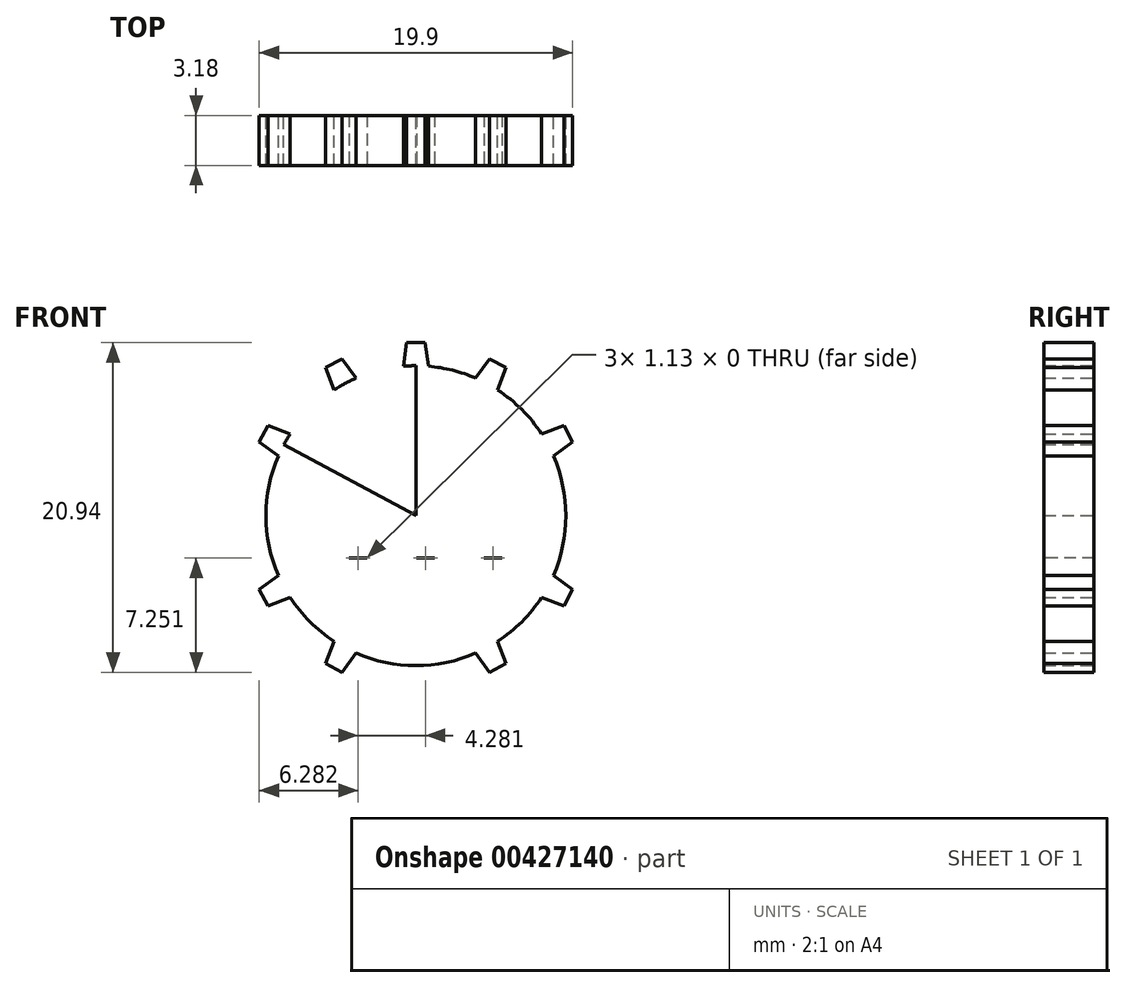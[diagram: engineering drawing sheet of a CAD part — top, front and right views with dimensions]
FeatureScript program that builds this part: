
annotation { "Feature Type Name" : "Feature", "Feature Type Description" : "" }
export const myFeature = defineFeature(function(context is Context, id is Id, definition is map)
    precondition{}
    {
        {
            var Q0;
            Q0=qCreatedBy(makeId("Front.planeOp"),FACE);
            var sketch = newSketch(context, id + "F0", { "sketchPlane" : qUnion([Q0])});
            skCircle(sketch, "E0", {"center": v(0, 0) * mm, "radius": 9.52 * mm});
            skLineSegment(sketch, "E1", {"start": v(0, 13.24) * mm, "end": v(0, -13.24) * mm});
            skLineSegment(sketch, "E2", {"start": v(-13.24, 0) * mm, "end": v(13.24, 0) * mm});
            skLineSegment(sketch, "E3", {"start": v(0, 0) * mm, "end": v(-5.21, 9.68) * mm});
            skLineSegment(sketch, "E4", {"start": v(0, 0) * mm, "end": v(5.21, -9.68) * mm});
            skLineSegment(sketch, "E5", {"start": v(0, 0) * mm, "end": v(5.21, 9.68) * mm});
            skLineSegment(sketch, "E6", {"start": v(0, 0) * mm, "end": v(-5.21, -9.68) * mm});
            skLineSegment(sketch, "E7", {"start": v(0, 0) * mm, "end": v(-9.68, 5.21) * mm});
            skLineSegment(sketch, "E8", {"start": v(0, 0) * mm, "end": v(9.68, -5.21) * mm});
            skLineSegment(sketch, "E9", {"start": v(0, 0) * mm, "end": v(9.68, 5.21) * mm});
            skLineSegment(sketch, "E10", {"start": v(0, 0) * mm, "end": v(-9.68, -5.21) * mm});
            skLineSegment(sketch, "E11", {"start": v(-5.21, 9.68) * mm, "end": v(-5.73, 9.4) * mm});
            skLineSegment(sketch, "E12", {"start": v(-5.73, 9.4) * mm, "end": v(-5.2, 7.98) * mm});
            skLineSegment(sketch, "E13", {"start": v(-5.21, 9.68) * mm, "end": v(-4.7, 9.95) * mm});
            skLineSegment(sketch, "E14", {"start": v(-4.7, 9.95) * mm, "end": v(-3.8, 8.73) * mm});
            skLineSegment(sketch, "E15", {"start": v(-9.68, 5.21) * mm, "end": v(-9.4, 5.73) * mm});
            skLineSegment(sketch, "E16", {"start": v(-9.68, 5.21) * mm, "end": v(-9.95, 4.7) * mm});
            skLineSegment(sketch, "E17", {"start": v(-9.4, 5.73) * mm, "end": v(-7.98, 5.2) * mm});
            skLineSegment(sketch, "E18", {"start": v(-9.95, 4.7) * mm, "end": v(-8.73, 3.8) * mm});
            skLineSegment(sketch, "E19", {"start": v(5.21, 9.68) * mm, "end": v(4.7, 9.95) * mm});
            skLineSegment(sketch, "E20", {"start": v(5.21, 9.68) * mm, "end": v(5.73, 9.4) * mm});
            skLineSegment(sketch, "E21", {"start": v(4.7, 9.95) * mm, "end": v(3.8, 8.73) * mm});
            skLineSegment(sketch, "E22", {"start": v(5.73, 9.4) * mm, "end": v(5.2, 7.98) * mm});
            skLineSegment(sketch, "E23", {"start": v(9.68, 5.21) * mm, "end": v(9.4, 5.73) * mm});
            skLineSegment(sketch, "E24", {"start": v(9.68, 5.21) * mm, "end": v(9.95, 4.7) * mm});
            skLineSegment(sketch, "E25", {"start": v(9.4, 5.73) * mm, "end": v(7.98, 5.2) * mm});
            skLineSegment(sketch, "E26", {"start": v(9.95, 4.7) * mm, "end": v(8.73, 3.8) * mm});
            skLineSegment(sketch, "E27", {"start": v(0, 10.99) * mm, "end": v(-0.59, 10.99) * mm});
            skLineSegment(sketch, "E28", {"start": v(0, 10.99) * mm, "end": v(0.59, 10.99) * mm});
            skLineSegment(sketch, "E29", {"start": v(0.59, 10.99) * mm, "end": v(0.8, 9.5) * mm});
            skLineSegment(sketch, "E30", {"start": v(-0.59, 10.99) * mm, "end": v(-0.8, 9.5) * mm});
            skLineSegment(sketch, "E31", {"start": v(0, 10.99) * mm, "end": v(0, 9.52) * mm});
            skLineSegment(sketch, "E32", {"start": v(-5.21, 9.68) * mm, "end": v(-4.52, 8.39) * mm});
            skLineSegment(sketch, "E33", {"start": v(-9.52, 0) * mm, "end": v(-10.99, 0) * mm});
            skLineSegment(sketch, "E34", {"start": v(-10.99, 0) * mm, "end": v(-10.99, -0.59) * mm});
            skLineSegment(sketch, "E35", {"start": v(-10.99, 0) * mm, "end": v(-10.99, 0.59) * mm});
            skLineSegment(sketch, "E36", {"start": v(-10.99, -0.59) * mm, "end": v(-9.5, -0.8) * mm});
            skLineSegment(sketch, "E37", {"start": v(-10.99, 0.59) * mm, "end": v(-9.5, 0.8) * mm});
            skLineSegment(sketch, "E38", {"start": v(9.52, 0) * mm, "end": v(10.99, 0) * mm});
            skLineSegment(sketch, "E39", {"start": v(10.99, 0) * mm, "end": v(10.99, 0.59) * mm});
            skLineSegment(sketch, "E40", {"start": v(10.99, 0) * mm, "end": v(10.99, -0.59) * mm});
            skLineSegment(sketch, "E41", {"start": v(10.99, 0.59) * mm, "end": v(9.5, 0.8) * mm});
            skLineSegment(sketch, "E42", {"start": v(10.99, -0.59) * mm, "end": v(9.5, -0.8) * mm});
            skLineSegment(sketch, "E43", {"start": v(9.68, -5.21) * mm, "end": v(9.95, -4.7) * mm});
            skLineSegment(sketch, "E44", {"start": v(9.68, -5.21) * mm, "end": v(9.4, -5.73) * mm});
            skLineSegment(sketch, "E45", {"start": v(9.95, -4.7) * mm, "end": v(8.73, -3.8) * mm});
            skLineSegment(sketch, "E46", {"start": v(9.4, -5.73) * mm, "end": v(7.98, -5.2) * mm});
            skLineSegment(sketch, "E47", {"start": v(-9.68, -5.21) * mm, "end": v(-9.95, -4.7) * mm});
            skLineSegment(sketch, "E48", {"start": v(-9.68, -5.21) * mm, "end": v(-9.4, -5.73) * mm});
            skLineSegment(sketch, "E49", {"start": v(-9.95, -4.7) * mm, "end": v(-8.73, -3.8) * mm});
            skLineSegment(sketch, "E50", {"start": v(-9.4, -5.73) * mm, "end": v(-7.98, -5.2) * mm});
            skLineSegment(sketch, "E51", {"start": v(-5.21, -9.68) * mm, "end": v(-5.73, -9.4) * mm});
            skLineSegment(sketch, "E52", {"start": v(-5.21, -9.68) * mm, "end": v(-4.7, -9.95) * mm});
            skLineSegment(sketch, "E53", {"start": v(-5.73, -9.4) * mm, "end": v(-5.2, -7.98) * mm});
            skLineSegment(sketch, "E54", {"start": v(-4.7, -9.95) * mm, "end": v(-3.8, -8.73) * mm});
            skLineSegment(sketch, "E55", {"start": v(0, -9.52) * mm, "end": v(0, -10.99) * mm});
            skLineSegment(sketch, "E56", {"start": v(0, -10.99) * mm, "end": v(-0.59, -10.99) * mm});
            skLineSegment(sketch, "E57", {"start": v(0, -10.99) * mm, "end": v(0.59, -10.99) * mm});
            skLineSegment(sketch, "E58", {"start": v(-0.59, -10.99) * mm, "end": v(-0.8, -9.5) * mm});
            skLineSegment(sketch, "E59", {"start": v(0.59, -10.99) * mm, "end": v(0.8, -9.5) * mm});
            skLineSegment(sketch, "E60", {"start": v(5.21, -9.68) * mm, "end": v(4.7, -9.95) * mm});
            skLineSegment(sketch, "E61", {"start": v(5.21, -9.68) * mm, "end": v(5.73, -9.4) * mm});
            skLineSegment(sketch, "E62", {"start": v(4.7, -9.95) * mm, "end": v(3.8, -8.73) * mm});
            skLineSegment(sketch, "E63", {"start": v(5.73, -9.4) * mm, "end": v(5.2, -7.98) * mm});
            skSolve(sketch);
        }
        {
            var Q0;
            {var subQ3=sQuery(id+"F0.wireOp",EDGE,"E0");var subQ5=makeQuery(id+"F0.imprint","INTERSECT",VERTEX,{"derivedFrom":[subQ3,sQuery(id+"F0.wireOp",EDGE,"E18")]});Q0=makeQuery(id+"F0.imprint","IMPRINT",FACE,{"disambiguationData":[TD([[makeQuery(id+"F0.imprint","IMPRINT",EDGE,{"disambiguationData":[TD([[subQ5,1.0]])],"derivedFrom":subQ3}),1.0]])]});}
            var Q1;
            {var subQ0=sQuery(id+"F0.wireOp",EDGE,"E3");Q1=makeQuery(id+"F0.imprint","IMPRINT",FACE,{"disambiguationData":[TD([[makeQuery(id+"F0.imprint","IMPRINT",EDGE,{"derivedFrom":subQ0}),1.0]])]});}
            var Q2;
            {var subQ0=sQuery(id+"F0.wireOp",EDGE,"E0");var subQ4=makeQuery(id+"F0.imprint","INTERSECT",VERTEX,{"derivedFrom":[subQ0,sQuery(id+"F0.wireOp",EDGE,"E21")]});Q2=makeQuery(id+"F0.imprint","IMPRINT",FACE,{"disambiguationData":[TD([[makeQuery(id+"F0.imprint","IMPRINT",EDGE,{"disambiguationData":[TD([[subQ4,1.0]])],"derivedFrom":subQ0}),1.0]])]});}
            var Q3;
            {var subQ0=sQuery(id+"F0.wireOp",EDGE,"E3");Q3=makeQuery(id+"F0.imprint","IMPRINT",FACE,{"disambiguationData":[TD([[makeQuery(id+"F0.imprint","IMPRINT",EDGE,{"derivedFrom":subQ0}),-1.0]])]});}
            var Q4;
            {var subQ0=sQuery(id+"F0.wireOp",EDGE,"E0");var subQ4=makeQuery(id+"F0.imprint","INTERSECT",VERTEX,{"derivedFrom":[subQ0,sQuery(id+"F0.wireOp",EDGE,"E25")]});Q4=makeQuery(id+"F0.imprint","IMPRINT",FACE,{"disambiguationData":[TD([[makeQuery(id+"F0.imprint","IMPRINT",EDGE,{"disambiguationData":[TD([[subQ4,1.0]])],"derivedFrom":subQ0}),1.0]])]});}
            var Q5;
            {var subQ3=sQuery(id+"F0.wireOp",EDGE,"E0");var subQ5=makeQuery(id+"F0.imprint","INTERSECT",VERTEX,{"derivedFrom":[subQ3,sQuery(id+"F0.wireOp",EDGE,"E26")]});Q5=makeQuery(id+"F0.imprint","IMPRINT",FACE,{"disambiguationData":[TD([[makeQuery(id+"F0.imprint","IMPRINT",EDGE,{"disambiguationData":[TD([[subQ5,1.0]])],"derivedFrom":subQ3}),1.0]])]});}
            var Q6;
            {var subQ1=sQuery(id+"F0.wireOp",EDGE,"E0");var subQ6=makeQuery(id+"F0.imprint","INTERSECT",VERTEX,{"derivedFrom":[subQ1,sQuery(id+"F0.wireOp",EDGE,"E45")]});Q6=makeQuery(id+"F0.imprint","IMPRINT",FACE,{"disambiguationData":[TD([[makeQuery(id+"F0.imprint","IMPRINT",EDGE,{"disambiguationData":[TD([[subQ6,1.0]])],"derivedFrom":subQ1}),1.0]])]});}
            var Q7;
            {var subQ0=sQuery(id+"F0.wireOp",EDGE,"E0");var subQ7=makeQuery(id+"F0.imprint","INTERSECT",VERTEX,{"derivedFrom":[subQ0,sQuery(id+"F0.wireOp",EDGE,"E63")]});Q7=makeQuery(id+"F0.imprint","IMPRINT",FACE,{"disambiguationData":[TD([[makeQuery(id+"F0.imprint","IMPRINT",EDGE,{"disambiguationData":[TD([[subQ7,1.0]])],"derivedFrom":subQ0}),1.0]])]});}
            var Q8;
            {var subQ0=sQuery(id+"F0.wireOp",EDGE,"E0");var subQ4=makeQuery(id+"F0.imprint","INTERSECT",VERTEX,{"derivedFrom":[subQ0,sQuery(id+"F0.wireOp",EDGE,"E59")]});Q8=makeQuery(id+"F0.imprint","IMPRINT",FACE,{"disambiguationData":[TD([[makeQuery(id+"F0.imprint","IMPRINT",EDGE,{"disambiguationData":[TD([[subQ4,-1.0]])],"derivedFrom":subQ0}),1.0]])]});}
            var Q9;
            {var subQ3=sQuery(id+"F0.wireOp",EDGE,"E0");var subQ6=makeQuery(id+"F0.imprint","INTERSECT",VERTEX,{"derivedFrom":[subQ3,sQuery(id+"F0.wireOp",EDGE,"E54")]});Q9=makeQuery(id+"F0.imprint","IMPRINT",FACE,{"disambiguationData":[TD([[makeQuery(id+"F0.imprint","IMPRINT",EDGE,{"disambiguationData":[TD([[subQ6,1.0]])],"derivedFrom":subQ3}),1.0]])]});}
            var Q10;
            {var subQ3=sQuery(id+"F0.wireOp",EDGE,"E0");var subQ6=makeQuery(id+"F0.imprint","INTERSECT",VERTEX,{"derivedFrom":[subQ3,sQuery(id+"F0.wireOp",EDGE,"E50")]});Q10=makeQuery(id+"F0.imprint","IMPRINT",FACE,{"disambiguationData":[TD([[makeQuery(id+"F0.imprint","IMPRINT",EDGE,{"disambiguationData":[TD([[subQ6,1.0]])],"derivedFrom":subQ3}),1.0]])]});}
            var Q11;
            {var subQ0=sQuery(id+"F0.wireOp",EDGE,"E0");var subQ6=makeQuery(id+"F0.imprint","INTERSECT",VERTEX,{"derivedFrom":[subQ0,sQuery(id+"F0.wireOp",EDGE,"E36")]});Q11=makeQuery(id+"F0.imprint","IMPRINT",FACE,{"disambiguationData":[TD([[makeQuery(id+"F0.imprint","IMPRINT",EDGE,{"disambiguationData":[TD([[subQ6,-1.0]])],"derivedFrom":subQ0}),1.0]])]});}
            var Q12;
            {var subQ0=sQuery(id+"F0.wireOp",EDGE,"E33");Q12=makeQuery(id+"F0.imprint","IMPRINT",FACE,{"disambiguationData":[TD([[makeQuery(id+"F0.imprint","IMPRINT",EDGE,{"derivedFrom":subQ0}),-1.0]])]});}
            var Q13;
            {var subQ0=sQuery(id+"F0.wireOp",EDGE,"E33");Q13=makeQuery(id+"F0.imprint","IMPRINT",FACE,{"disambiguationData":[TD([[makeQuery(id+"F0.imprint","IMPRINT",EDGE,{"derivedFrom":subQ0}),1.0]])]});}
            var Q14;
            {var subQ4=sQuery(id+"F0.wireOp",EDGE,"E16");Q14=makeQuery(id+"F0.imprint","IMPRINT",FACE,{"disambiguationData":[TD([[makeQuery(id+"F0.imprint","IMPRINT",EDGE,{"derivedFrom":subQ4}),1.0]])]});}
            var Q15;
            {var subQ4=sQuery(id+"F0.wireOp",EDGE,"E15");Q15=makeQuery(id+"F0.imprint","IMPRINT",FACE,{"disambiguationData":[TD([[makeQuery(id+"F0.imprint","IMPRINT",EDGE,{"derivedFrom":subQ4}),-1.0]])]});}
            var Q16;
            Q16=makeQuery(id+"F0.imprint","IMPRINT",FACE,{"disambiguationData":[TD([[makeQuery(id+"F0.imprint","IMPRINT",EDGE,{"derivedFrom":sQuery(id+"F0.wireOp",EDGE,"E11")}),1.0]])]});
            var Q17;
            Q17=makeQuery(id+"F0.imprint","IMPRINT",FACE,{"disambiguationData":[TD([[makeQuery(id+"F0.imprint","IMPRINT",EDGE,{"derivedFrom":sQuery(id+"F0.wireOp",EDGE,"E13")}),-1.0]])]});
            var Q18;
            Q18=makeQuery(id+"F0.imprint","IMPRINT",FACE,{"disambiguationData":[TD([[makeQuery(id+"F0.imprint","IMPRINT",EDGE,{"derivedFrom":sQuery(id+"F0.wireOp",EDGE,"E27")}),1.0]])]});
            var Q19;
            Q19=makeQuery(id+"F0.imprint","IMPRINT",FACE,{"disambiguationData":[TD([[makeQuery(id+"F0.imprint","IMPRINT",EDGE,{"derivedFrom":sQuery(id+"F0.wireOp",EDGE,"E28")}),-1.0]])]});
            var Q20;
            {var subQ4=sQuery(id+"F0.wireOp",EDGE,"E19");Q20=makeQuery(id+"F0.imprint","IMPRINT",FACE,{"disambiguationData":[TD([[makeQuery(id+"F0.imprint","IMPRINT",EDGE,{"derivedFrom":subQ4}),1.0]])]});}
            var Q21;
            {var subQ4=sQuery(id+"F0.wireOp",EDGE,"E20");Q21=makeQuery(id+"F0.imprint","IMPRINT",FACE,{"disambiguationData":[TD([[makeQuery(id+"F0.imprint","IMPRINT",EDGE,{"derivedFrom":subQ4}),-1.0]])]});}
            var Q22;
            {var subQ4=sQuery(id+"F0.wireOp",EDGE,"E23");Q22=makeQuery(id+"F0.imprint","IMPRINT",FACE,{"disambiguationData":[TD([[makeQuery(id+"F0.imprint","IMPRINT",EDGE,{"derivedFrom":subQ4}),1.0]])]});}
            var Q23;
            {var subQ4=sQuery(id+"F0.wireOp",EDGE,"E24");Q23=makeQuery(id+"F0.imprint","IMPRINT",FACE,{"disambiguationData":[TD([[makeQuery(id+"F0.imprint","IMPRINT",EDGE,{"derivedFrom":subQ4}),-1.0]])]});}
            var Q24;
            {var subQ0=sQuery(id+"F0.wireOp",EDGE,"E38");Q24=makeQuery(id+"F0.imprint","IMPRINT",FACE,{"disambiguationData":[TD([[makeQuery(id+"F0.imprint","IMPRINT",EDGE,{"derivedFrom":subQ0}),1.0]])]});}
            var Q25;
            {var subQ0=sQuery(id+"F0.wireOp",EDGE,"E38");Q25=makeQuery(id+"F0.imprint","IMPRINT",FACE,{"disambiguationData":[TD([[makeQuery(id+"F0.imprint","IMPRINT",EDGE,{"derivedFrom":subQ0}),-1.0]])]});}
            var Q26;
            {var subQ4=sQuery(id+"F0.wireOp",EDGE,"E43");Q26=makeQuery(id+"F0.imprint","IMPRINT",FACE,{"disambiguationData":[TD([[makeQuery(id+"F0.imprint","IMPRINT",EDGE,{"derivedFrom":subQ4}),1.0]])]});}
            var Q27;
            {var subQ4=sQuery(id+"F0.wireOp",EDGE,"E44");Q27=makeQuery(id+"F0.imprint","IMPRINT",FACE,{"disambiguationData":[TD([[makeQuery(id+"F0.imprint","IMPRINT",EDGE,{"derivedFrom":subQ4}),-1.0]])]});}
            var Q28;
            {var subQ4=sQuery(id+"F0.wireOp",EDGE,"E61");Q28=makeQuery(id+"F0.imprint","IMPRINT",FACE,{"disambiguationData":[TD([[makeQuery(id+"F0.imprint","IMPRINT",EDGE,{"derivedFrom":subQ4}),1.0]])]});}
            var Q29;
            {var subQ4=sQuery(id+"F0.wireOp",EDGE,"E60");Q29=makeQuery(id+"F0.imprint","IMPRINT",FACE,{"disambiguationData":[TD([[makeQuery(id+"F0.imprint","IMPRINT",EDGE,{"derivedFrom":subQ4}),-1.0]])]});}
            var Q30;
            {var subQ0=sQuery(id+"F0.wireOp",EDGE,"E55");Q30=makeQuery(id+"F0.imprint","IMPRINT",FACE,{"disambiguationData":[TD([[makeQuery(id+"F0.imprint","IMPRINT",EDGE,{"derivedFrom":subQ0}),1.0]])]});}
            var Q31;
            {var subQ0=sQuery(id+"F0.wireOp",EDGE,"E55");Q31=makeQuery(id+"F0.imprint","IMPRINT",FACE,{"disambiguationData":[TD([[makeQuery(id+"F0.imprint","IMPRINT",EDGE,{"derivedFrom":subQ0}),-1.0]])]});}
            var Q32;
            {var subQ4=sQuery(id+"F0.wireOp",EDGE,"E52");Q32=makeQuery(id+"F0.imprint","IMPRINT",FACE,{"disambiguationData":[TD([[makeQuery(id+"F0.imprint","IMPRINT",EDGE,{"derivedFrom":subQ4}),1.0]])]});}
            var Q33;
            {var subQ4=sQuery(id+"F0.wireOp",EDGE,"E51");Q33=makeQuery(id+"F0.imprint","IMPRINT",FACE,{"disambiguationData":[TD([[makeQuery(id+"F0.imprint","IMPRINT",EDGE,{"derivedFrom":subQ4}),-1.0]])]});}
            var Q34;
            {var subQ4=sQuery(id+"F0.wireOp",EDGE,"E48");Q34=makeQuery(id+"F0.imprint","IMPRINT",FACE,{"disambiguationData":[TD([[makeQuery(id+"F0.imprint","IMPRINT",EDGE,{"derivedFrom":subQ4}),1.0]])]});}
            var Q35;
            {var subQ4=sQuery(id+"F0.wireOp",EDGE,"E47");Q35=makeQuery(id+"F0.imprint","IMPRINT",FACE,{"disambiguationData":[TD([[makeQuery(id+"F0.imprint","IMPRINT",EDGE,{"derivedFrom":subQ4}),-1.0]])]});}
            extrude(context, id + "F1", {"entities" : qUnion([Q0, Q1, Q2, Q3, Q4, Q5, Q6, Q7, Q8, Q9, Q10, Q11, Q12, Q13, Q14, Q15, Q16, Q17, Q18, Q19, Q20, Q21, Q22, Q23, Q24, Q25, Q26, Q27, Q28, Q29, Q30, Q31, Q32, Q33, Q34, Q35]), "depth" : 3.17 * mm});
        }
        {
            var Q0;
            Q0=makeQuery(id+"F1.opExtrude","CAP_FACE",FACE,{"disambiguationData":[OSD([sQuery(id+"F0.wireOp",EDGE,"E0"),sQuery(id+"F0.wireOp",EDGE,"E11"),sQuery(id+"F0.wireOp",EDGE,"E12"),sQuery(id+"F0.wireOp",EDGE,"E13"),sQuery(id+"F0.wireOp",EDGE,"E14"),sQuery(id+"F0.wireOp",EDGE,"E15"),sQuery(id+"F0.wireOp",EDGE,"E16"),sQuery(id+"F0.wireOp",EDGE,"E17"),sQuery(id+"F0.wireOp",EDGE,"E18"),sQuery(id+"F0.wireOp",EDGE,"E19"),sQuery(id+"F0.wireOp",EDGE,"E20"),sQuery(id+"F0.wireOp",EDGE,"E21"),sQuery(id+"F0.wireOp",EDGE,"E22"),sQuery(id+"F0.wireOp",EDGE,"E23"),sQuery(id+"F0.wireOp",EDGE,"E24"),sQuery(id+"F0.wireOp",EDGE,"E25"),sQuery(id+"F0.wireOp",EDGE,"E26"),sQuery(id+"F0.wireOp",EDGE,"E27"),sQuery(id+"F0.wireOp",EDGE,"E28"),sQuery(id+"F0.wireOp",EDGE,"E29"),sQuery(id+"F0.wireOp",EDGE,"E30"),sQuery(id+"F0.wireOp",EDGE,"E34"),sQuery(id+"F0.wireOp",EDGE,"E35"),sQuery(id+"F0.wireOp",EDGE,"E36"),sQuery(id+"F0.wireOp",EDGE,"E37"),sQuery(id+"F0.wireOp",EDGE,"E39"),sQuery(id+"F0.wireOp",EDGE,"E40"),sQuery(id+"F0.wireOp",EDGE,"E41"),sQuery(id+"F0.wireOp",EDGE,"E42"),sQuery(id+"F0.wireOp",EDGE,"E43"),sQuery(id+"F0.wireOp",EDGE,"E44"),sQuery(id+"F0.wireOp",EDGE,"E45"),sQuery(id+"F0.wireOp",EDGE,"E46"),sQuery(id+"F0.wireOp",EDGE,"E47"),sQuery(id+"F0.wireOp",EDGE,"E48"),sQuery(id+"F0.wireOp",EDGE,"E49"),sQuery(id+"F0.wireOp",EDGE,"E50"),sQuery(id+"F0.wireOp",EDGE,"E51"),sQuery(id+"F0.wireOp",EDGE,"E52"),sQuery(id+"F0.wireOp",EDGE,"E53"),sQuery(id+"F0.wireOp",EDGE,"E54"),sQuery(id+"F0.wireOp",EDGE,"E56"),sQuery(id+"F0.wireOp",EDGE,"E57"),sQuery(id+"F0.wireOp",EDGE,"E58"),sQuery(id+"F0.wireOp",EDGE,"E59"),sQuery(id+"F0.wireOp",EDGE,"E60"),sQuery(id+"F0.wireOp",EDGE,"E61"),sQuery(id+"F0.wireOp",EDGE,"E62"),sQuery(id+"F0.wireOp",EDGE,"E63")])],"isStart":false});
            var sketch = newSketch(context, id + "F2", { "sketchPlane" : qUnion([Q0])});
            skLineSegment(sketch, "E64", {"start": v(-0.14, -2.7) * mm, "end": v(-6.2, -2.7) * mm});
            skLineSegment(sketch, "E65", {"start": v(-6.2, -2.7) * mm, "end": v(-6.2, 2.7) * mm});
            skLineSegment(sketch, "E66", {"start": v(-6.2, 2.7) * mm, "end": v(5.93, 2.7) * mm});
            skLineSegment(sketch, "E67", {"start": v(5.93, 2.7) * mm, "end": v(5.93, -2.7) * mm});
            skLineSegment(sketch, "E68", {"start": v(5.93, -2.7) * mm, "end": v(-0.14, -2.7) * mm});
            skText(sketch, "E69", { "text": "111\n", "fontName": "OpenSans-Bold.ttf"});
            skLineSegment(sketch, "E70", {"start": v(-6.2, 0) * mm, "end": v(-10.99, 0) * mm});
            skLineSegment(sketch, "E71", {"start": v(5.93, 0) * mm, "end": v(10.99, 0) * mm});
            const initialGuessF2  = {"E69": [-0.0062, -0.0027, 1, 0, 0.0054]};
            skSetInitialGuess(sketch, initialGuessF2);
            skSolve(sketch);
        }
        {
            var Q0;
            Q0=makeQuery(id+"F2.imprint","IMPRINT",FACE,{"disambiguationData":[TD([[makeQuery(id+"F2.imprint","IMPRINT",EDGE,{"derivedFrom":sQuery(id+"F2.wireOp",EDGE,"E69.sketch_text.stroke-0")}),-1.0]])]});
            var Q1;
            Q1=makeQuery(id+"F2.imprint","IMPRINT",FACE,{"disambiguationData":[TD([[makeQuery(id+"F2.imprint","IMPRINT",EDGE,{"derivedFrom":sQuery(id+"F2.wireOp",EDGE,"E69.sketch_text.stroke-10")}),-1.0]])]});
            var Q2;
            Q2=makeQuery(id+"F2.imprint","IMPRINT",FACE,{"disambiguationData":[TD([[makeQuery(id+"F2.imprint","IMPRINT",EDGE,{"derivedFrom":sQuery(id+"F2.wireOp",EDGE,"E69.sketch_text.stroke-20")}),-1.0]])]});
            extrude(context, id + "F3", {"entities" : qUnion([Q0, Q1, Q2]), "operationType" : NewBodyOperationType.REMOVE, "oppositeDirection" : true, "depth" : 25.4 * mm});
        }
    });
